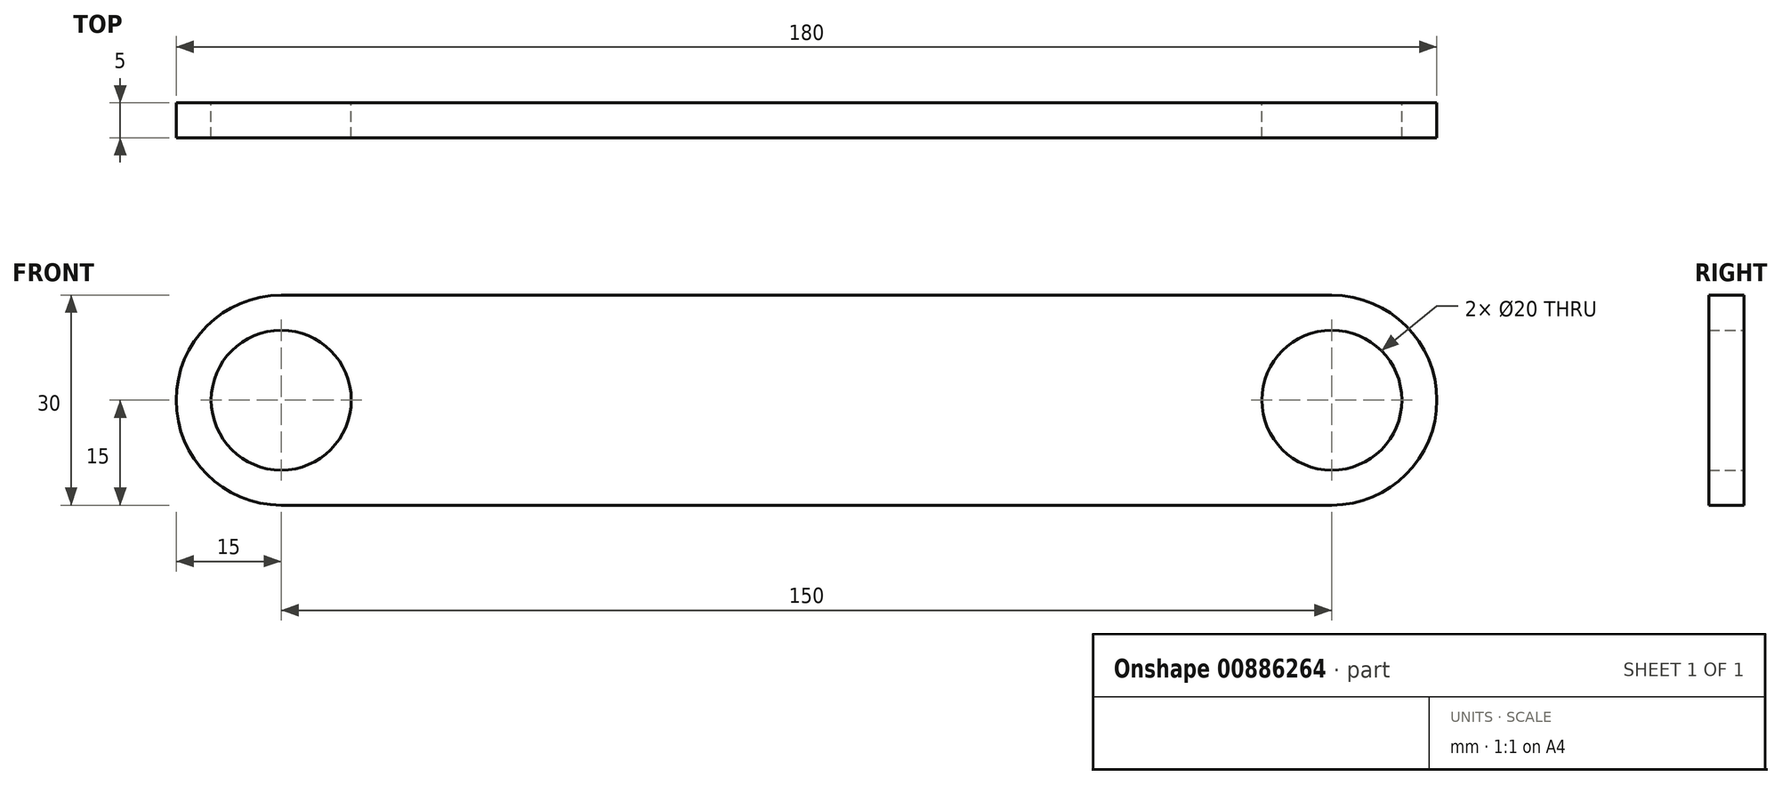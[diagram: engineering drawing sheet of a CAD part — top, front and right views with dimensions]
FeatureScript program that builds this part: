
annotation { "Feature Type Name" : "Feature", "Feature Type Description" : "" }
export const myFeature = defineFeature(function(context is Context, id is Id, definition is map)
    precondition{}
    {
        {
            var Q0;
            Q0=qCreatedBy(makeId("Front.planeOp"),FACE);
            var sketch = newSketch(context, id + "F0", { "sketchPlane" : qUnion([Q0])});
            skLineSegment(sketch, "E0.bottom", {"start": v(-75, 15) * mm, "end": v(75, 15) * mm});
            skLineSegment(sketch, "E0.top", {"start": v(-75, -15) * mm, "end": v(75, -15) * mm});
            skLineSegment(sketch, "E0.left", {"start": v(-75, 15) * mm, "end": v(-75, -15) * mm});
            skLineSegment(sketch, "E0.right", {"start": v(75, 15) * mm, "end": v(75, -15) * mm});
            skPoint(sketch, "E0.middle", {"position": v(0, 0) * mm});
            skArc(sketch, "E1", {"start": v(-75, 15) * mm, "mid": v(-90, 0) * mm, "end": v(-75, -15) * mm});
            skArc(sketch, "E2", {"start": v(75, 15) * mm, "mid": v(90, 0) * mm, "end": v(75, -15) * mm});
            skCircle(sketch, "E3", {"center": v(-75, 0) * mm, "radius": 10 * mm});
            skCircle(sketch, "E4", {"center": v(75, 0) * mm, "radius": 10 * mm});
            skSolve(sketch);
        }
        {
            var Q0;
            Q0 = qSketchRegion(id + "F0", true);
            extrude(context, id + "F1", {"entities" : qUnion([Q0]), "depth" : 5 * mm, "offsetDistance" : 25 * mm, "symmetric" : true});
        }
    });
